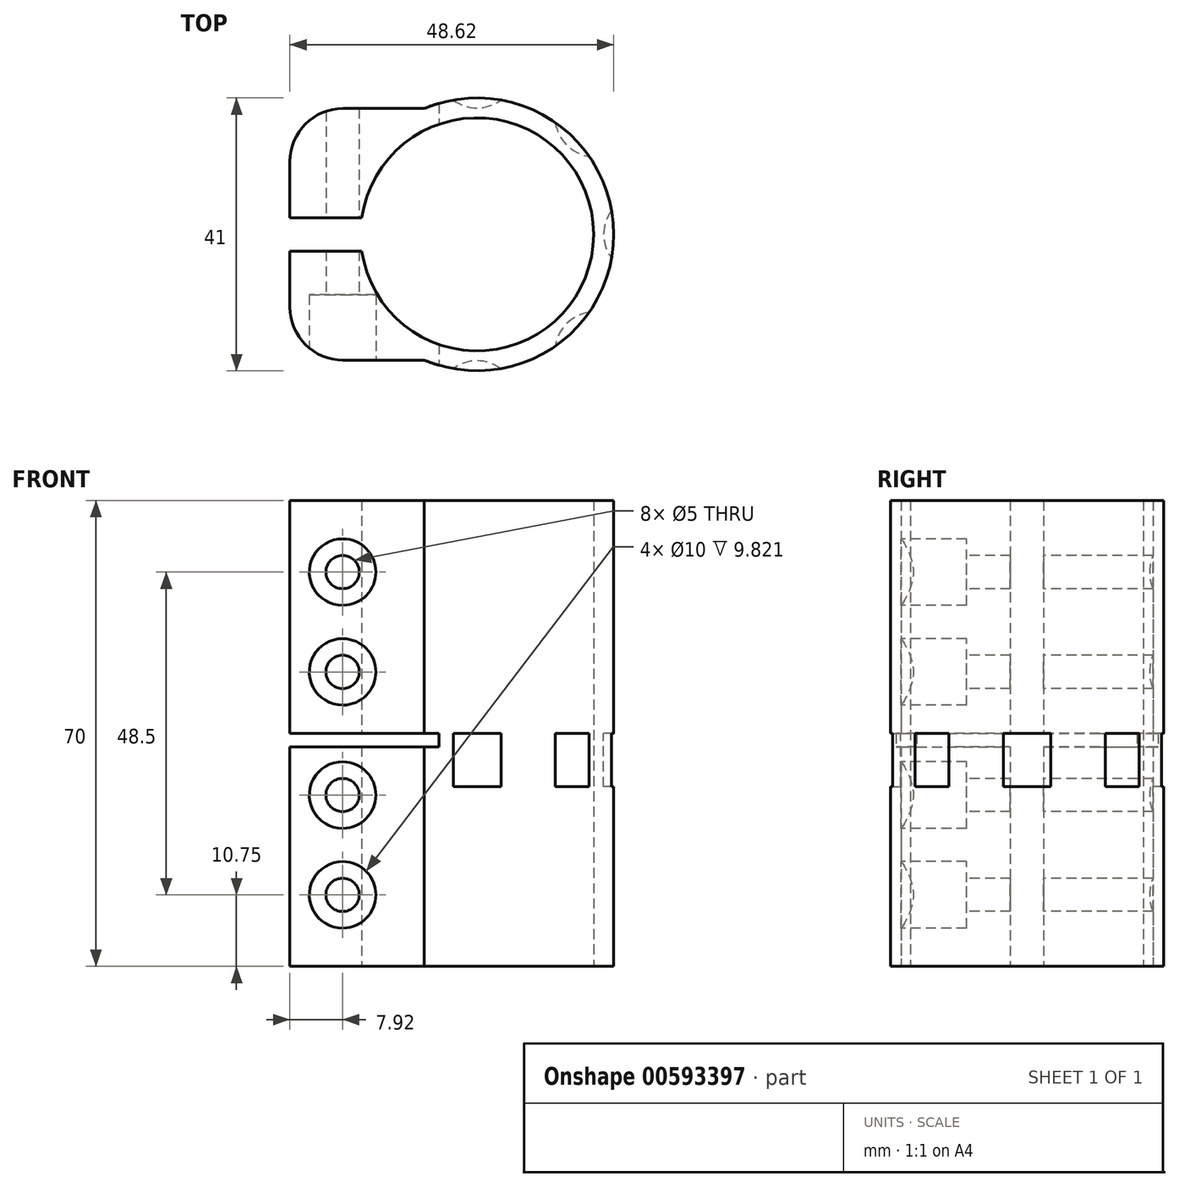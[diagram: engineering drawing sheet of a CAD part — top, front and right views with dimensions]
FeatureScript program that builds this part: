
annotation { "Feature Type Name" : "Feature", "Feature Type Description" : "" }
export const myFeature = defineFeature(function(context is Context, id is Id, definition is map)
    precondition{}
    {
        {
            var Q0;
            Q0=qCreatedBy(makeId("Top.planeOp"),FACE);
            var sketch = newSketch(context, id + "F0", { "sketchPlane" : qUnion([Q0])});
            skArc(sketch, "E0", {"start": v(-7.92, -18.9) * mm, "mid": v(20.5, 0) * mm, "end": v(-7.92, 18.9) * mm});
            skArc(sketch, "E1", {"start": v(-17.32, -2.5) * mm, "mid": v(17.5, 0) * mm, "end": v(-17.32, 2.5) * mm});
            skLineSegment(sketch, "E2", {"start": v(-7.92, 18.9) * mm, "end": v(-20.12, 18.9) * mm});
            skLineSegment(sketch, "E3", {"start": v(-17.32, 2.5) * mm, "end": v(-28.12, 2.5) * mm});
            skLineSegment(sketch, "E4", {"start": v(-28.12, 10.9) * mm, "end": v(-28.12, 2.5) * mm});
            skPoint(sketch, "E5.visualSharp", {"position": v(-28.12, 18.9) * mm});
            skArc(sketch, "E5.filletArc", {"start": v(-20.12, 18.9) * mm, "mid": v(-25.78, 16.57) * mm, "end": v(-28.12, 10.9) * mm});
            skLineSegment(sketch, "E6", {"start": v(0, 0) * mm, "end": v(45.49, 0) * mm, "construction": true});
            skPoint(sketch, "E7.newPointA", {"position": v(-20.12, 18.9) * mm});
            skPoint(sketch, "E7.newPointB", {"position": v(-28.12, 10.9) * mm});
            skLineSegment(sketch, "E8.MirrorCS", {"start": v(-17.32, -2.5) * mm, "end": v(-28.12, -2.5) * mm});
            skLineSegment(sketch, "E9.MirrorCS", {"start": v(-7.92, -18.9) * mm, "end": v(-20.12, -18.9) * mm});
            skArc(sketch, "E10.MirrorCS", {"start": v(-20.12, -18.9) * mm, "mid": v(-25.78, -16.57) * mm, "end": v(-28.12, -10.9) * mm});
            skLineSegment(sketch, "E11.MirrorCS", {"start": v(-28.12, -10.9) * mm, "end": v(-28.12, -2.5) * mm});
            skSolve(sketch);
        }
        {
            var Q0;
            Q0 = qSketchRegion(id + "F0", true);
            extrude(context, id + "F1", {"entities" : qUnion([Q0]), "depth" : 70 * mm, "offsetDistance" : 25 * mm, "symmetric" : true});
        }
        {
            var Q0;
            Q0=makeQuery(id+"F1.opExtrude","SWEPT_FACE",FACE,{"disambiguationData":[OSD([sQuery(id+"F0.wireOp",EDGE,"E9.MirrorCS")])]});
            var sketch = newSketch(context, id + "F2", { "sketchPlane" : qUnion([Q0])});
            skPoint(sketch, "E12", {"position": v(-20.2, -24.25) * mm});
            skPoint(sketch, "E13", {"position": v(-20.2, -9.25) * mm});
            skPoint(sketch, "E14", {"position": v(-20.2, 9.25) * mm});
            skPoint(sketch, "E15", {"position": v(-20.2, 24.25) * mm});
            skSolve(sketch);
        }
        {
            var Q0;
            Q0=sQuery(id+"F2.wireOp",VERTEX,"E12");
            var Q1;
            Q1=sQuery(id+"F2.wireOp",VERTEX,"E13");
            var Q2;
            Q2=sQuery(id+"F2.wireOp",VERTEX,"E14");
            var Q3;
            Q3=sQuery(id+"F2.wireOp",VERTEX,"E15");
            var Q4;
            Q4=makeQuery(id+"F1.opExtrude","SWEPT_BODY",BODY,{"disambiguationData":[OSD([sQuery(id+"F0.wireOp",EDGE,"E0"),sQuery(id+"F0.wireOp",EDGE,"E1"),sQuery(id+"F0.wireOp",EDGE,"E2"),sQuery(id+"F0.wireOp",EDGE,"E3"),sQuery(id+"F0.wireOp",EDGE,"E4"),sQuery(id+"F0.wireOp",EDGE,"E5.filletArc"),sQuery(id+"F0.wireOp",EDGE,"E9.MirrorCS"),sQuery(id+"F0.wireOp",EDGE,"E10.MirrorCS"),sQuery(id+"F0.wireOp",EDGE,"E11.MirrorCS"),sQuery(id+"F0.wireOp",EDGE,"E8.MirrorCS")])]});
            hole(context, id + "F3", {"style" : HoleStyle.C_BORE, "endStyle" : HoleEndStyle.THROUGH, "holeDiameter" : 5 * mm, "cBoreDiameter" : 10 * mm, "cBoreDepth" : 8 * mm, "majorDiameter" : 5 * mm, "isTappedThrough" : true, "tappedDepth" : 12 * mm, "tapClearance" : 3, "locations" : qUnion([Q0, Q1, Q2, Q3]), "scope" : qUnion([Q4])});
        }
        {
            var Q0;
            Q0=qCreatedBy(makeId("Front.planeOp"),FACE);
            var sketch = newSketch(context, id + "F4", { "sketchPlane" : qUnion([Q0])});
            skLineSegment(sketch, "E16.bottom", {"start": v(-28.12, 0) * mm, "end": v(-5.72, 0) * mm});
            skLineSegment(sketch, "E16.top", {"start": v(-28.12, -2) * mm, "end": v(-5.72, -2) * mm});
            skLineSegment(sketch, "E16.left", {"start": v(-28.12, 0) * mm, "end": v(-28.12, -2) * mm});
            skLineSegment(sketch, "E16.right", {"start": v(-5.72, 0) * mm, "end": v(-5.72, -2) * mm});
            skSolve(sketch);
        }
        {
            var Q0;
            Q0 = qSketchRegion(id + "F4", true);
            extrude(context, id + "F5", {"entities" : qUnion([Q0]), "operationType" : NewBodyOperationType.REMOVE, "oppositeDirection" : true, "depth" : 50 * mm, "offsetDistance" : 25 * mm, "symmetric" : true});
        }
        {
            var Q0;
            Q0=qCreatedBy(makeId("Top.planeOp"),FACE);
            var sketch = newSketch(context, id + "F6", { "sketchPlane" : qUnion([Q0])});
            skCircle(sketch, "E17", {"center": v(0, -25) * mm, "radius": 6 * mm});
            skPoint(sketch, "E18.end.orphan", {"position": v(35.84, -35.93) * mm});
            skPoint(sketch, "E19.orphan", {"position": v(35.36, -35.93) * mm});
            skCircle(sketch, "E20.1.0", {"center": v(17.68, -17.68) * mm, "radius": 6 * mm});
            skCircle(sketch, "E20.2.0", {"center": v(25, 0) * mm, "radius": 6 * mm});
            skCircle(sketch, "E20.3.0", {"center": v(17.68, 17.68) * mm, "radius": 6 * mm});
            skCircle(sketch, "E20.4.0", {"center": v(0, 25) * mm, "radius": 6 * mm});
            skPoint(sketch, "E20.center", {"position": v(0, 0) * mm});
            skLineSegment(sketch, "E20.anchor1", {"start": v(0, 0) * mm, "end": v(0, -25) * mm, "construction": true});
            skLineSegment(sketch, "E20.anchor2", {"start": v(0, 0) * mm, "end": v(0, 25) * mm, "construction": true});
            skSolve(sketch);
        }
        {
            var Q0;
            Q0 = qSketchRegion(id + "F6", true);
            extrude(context, id + "F7", {"entities" : qUnion([Q0]), "operationType" : NewBodyOperationType.REMOVE, "oppositeDirection" : true, "depth" : 8 * mm, "offsetDistance" : 25 * mm});
        }
    });
